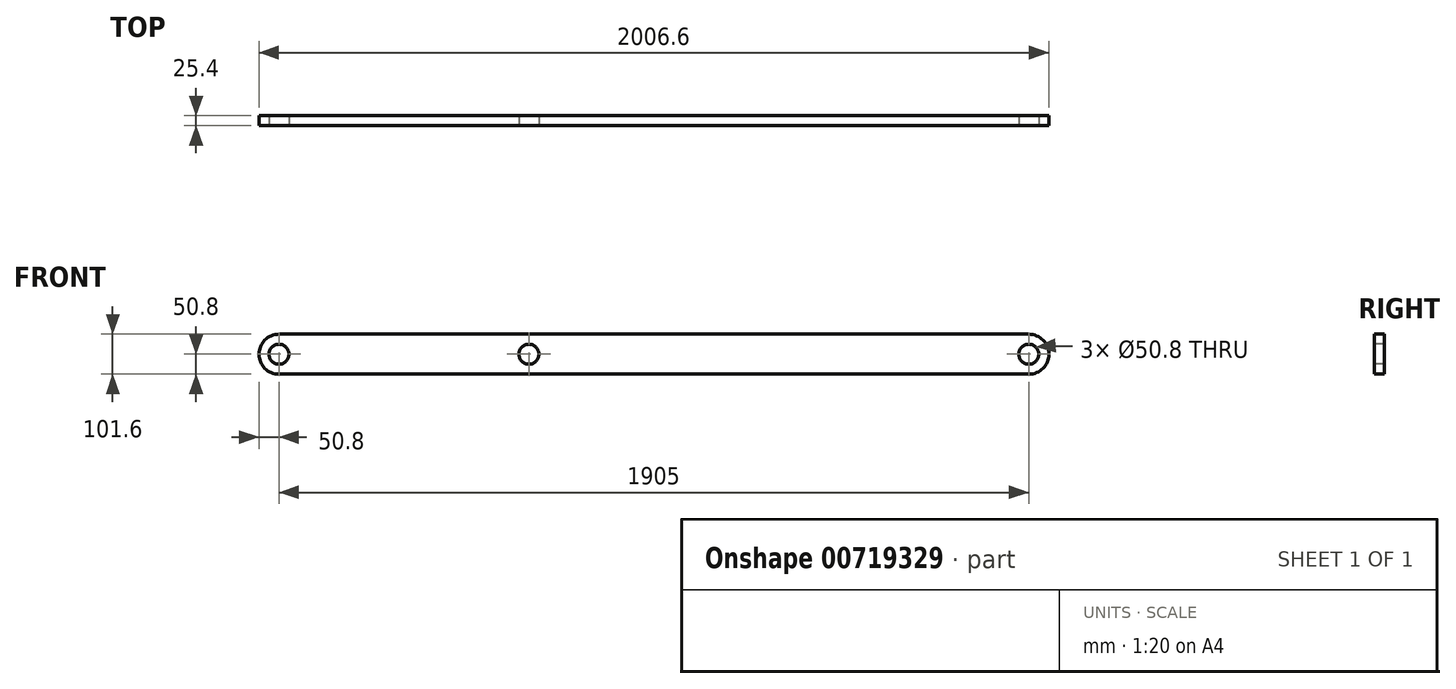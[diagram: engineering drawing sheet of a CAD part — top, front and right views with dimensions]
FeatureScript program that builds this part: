
annotation { "Feature Type Name" : "Feature", "Feature Type Description" : "" }
export const myFeature = defineFeature(function(context is Context, id is Id, definition is map)
    precondition{}
    {
        {
            var Q0;
            Q0=qCreatedBy(makeId("Front.planeOp"),FACE);
            var sketch = newSketch(context, id + "F0", { "sketchPlane" : qUnion([Q0])});
            skLineSegment(sketch, "E0.bottom", {"start": v(-952.5, 50.8) * mm, "end": v(952.5, 50.8) * mm});
            skLineSegment(sketch, "E0.top", {"start": v(-952.5, -50.8) * mm, "end": v(952.5, -50.8) * mm});
            skArc(sketch, "E1", {"start": v(-952.5, 50.8) * mm, "mid": v(-1003.3, 0) * mm, "end": v(-952.5, -50.8) * mm});
            skArc(sketch, "E2", {"start": v(952.5, -50.8) * mm, "mid": v(1003.3, 0) * mm, "end": v(952.5, 50.8) * mm});
            skSolve(sketch);
        }
        {
            var Q0;
            Q0 = qSketchRegion(id + "F0", true);
            extrude(context, id + "F1", {"entities" : qUnion([Q0]), "endBound" : BoundingType.SYMMETRIC, "depth" : 25.4 * mm, "offsetDistance" : 25.4 * mm});
        }
        {
            var Q0;
            Q0=makeQuery(id+"F1.opExtrude","CAP_FACE",FACE,{"disambiguationData":[OSD([sQuery(id+"F0.wireOp",EDGE,"E0.bottom"),sQuery(id+"F0.wireOp",EDGE,"E0.top"),sQuery(id+"F0.wireOp",EDGE,"E1"),sQuery(id+"F0.wireOp",EDGE,"E2")])],"isStart":false});
            var sketch = newSketch(context, id + "F2", { "sketchPlane" : qUnion([Q0])});
            skCircle(sketch, "E3", {"center": v(-952.5, 0) * mm, "radius": 25.4 * mm});
            skCircle(sketch, "E4", {"center": v(952.5, 0) * mm, "radius": 25.4 * mm});
            skCircle(sketch, "E5", {"center": v(-317.5, 0) * mm, "radius": 25.4 * mm});
            skSolve(sketch);
        }
        {
            var Q0;
            Q0 = qSketchRegion(id + "F2", true);
            extrude(context, id + "F3", {"entities" : qUnion([Q0]), "operationType" : NewBodyOperationType.REMOVE, "endBound" : BoundingType.THROUGH_ALL, "oppositeDirection" : true, "depth" : 25.4 * mm, "offsetDistance" : 25.4 * mm});
        }
    });
